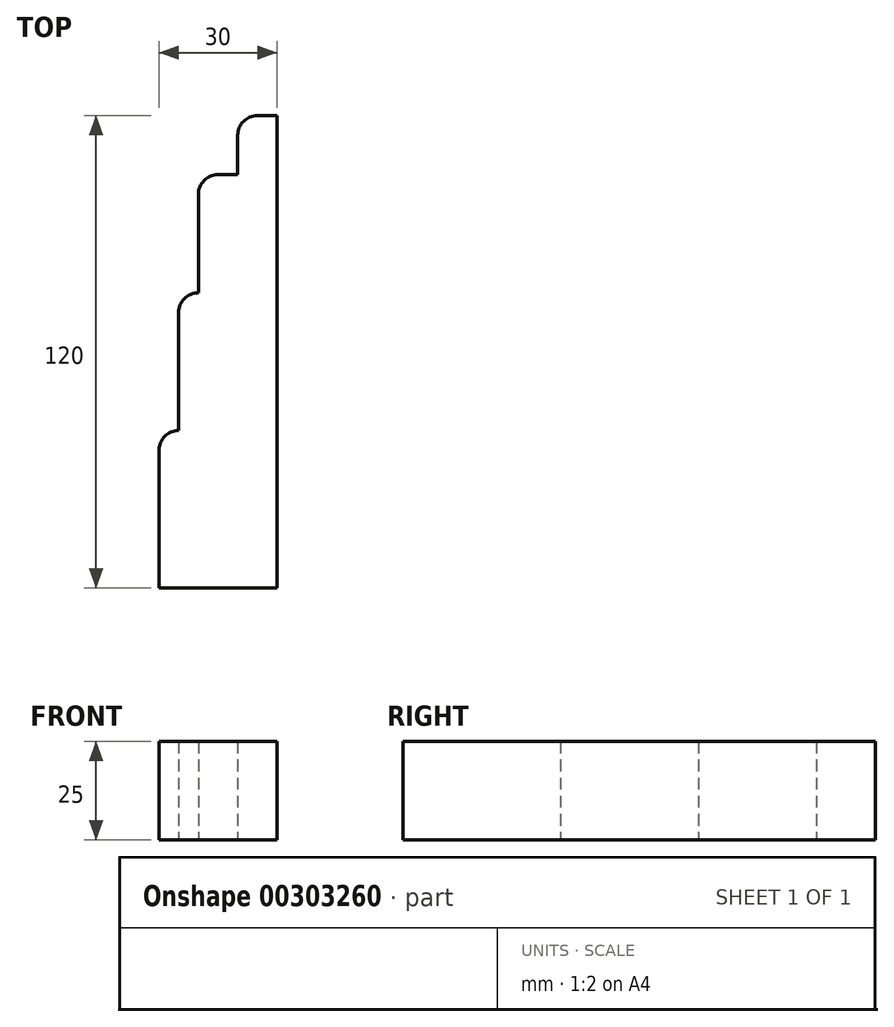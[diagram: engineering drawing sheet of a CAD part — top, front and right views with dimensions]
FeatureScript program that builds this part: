
annotation { "Feature Type Name" : "Feature", "Feature Type Description" : "" }
export const myFeature = defineFeature(function(context is Context, id is Id, definition is map)
    precondition{}
    {
        {
            var Q0;
            Q0=qCreatedBy(makeId("Top.planeOp"),FACE);
            var sketch = newSketch(context, id + "F0", { "sketchPlane" : qUnion([Q0])});
            skLineSegment(sketch, "E0", {"start": v(0, 0) * mm, "end": v(30, 0) * mm});
            skLineSegment(sketch, "E1", {"start": v(30, 0) * mm, "end": v(30, 120) * mm});
            skLineSegment(sketch, "E2", {"start": v(30, 120) * mm, "end": v(25, 120) * mm});
            skLineSegment(sketch, "E3", {"start": v(0, 0) * mm, "end": v(0, 35) * mm});
            skLineSegment(sketch, "E4", {"start": v(5, 40) * mm, "end": v(5, 40) * mm});
            skLineSegment(sketch, "E5", {"start": v(5, 40) * mm, "end": v(5, 70) * mm});
            skLineSegment(sketch, "E6", {"start": v(10, 75) * mm, "end": v(10, 75) * mm});
            skLineSegment(sketch, "E7", {"start": v(10, 75) * mm, "end": v(10, 100) * mm});
            skLineSegment(sketch, "E8", {"start": v(15, 105) * mm, "end": v(20, 105) * mm});
            skLineSegment(sketch, "E9", {"start": v(20, 105) * mm, "end": v(20, 115) * mm});
            skPoint(sketch, "E10.visualSharp", {"position": v(0, 40) * mm});
            skArc(sketch, "E10.filletArc", {"start": v(5, 40) * mm, "mid": v(1.46, 38.54) * mm, "end": v(0, 35) * mm});
            skPoint(sketch, "E11.visualSharp", {"position": v(5, 75) * mm});
            skArc(sketch, "E11.filletArc", {"start": v(10, 75) * mm, "mid": v(6.46, 73.54) * mm, "end": v(5, 70) * mm});
            skPoint(sketch, "E12.visualSharp", {"position": v(10, 105) * mm});
            skArc(sketch, "E12.filletArc", {"start": v(15, 105) * mm, "mid": v(11.46, 103.54) * mm, "end": v(10, 100) * mm});
            skPoint(sketch, "E13.visualSharp", {"position": v(20, 120) * mm});
            skArc(sketch, "E13.filletArc", {"start": v(25, 120) * mm, "mid": v(21.46, 118.54) * mm, "end": v(20, 115) * mm});
            skSolve(sketch);
        }
        {
            var Q0;
            Q0 = qSketchRegion(id + "F0", true);
            extrude(context, id + "F1", {"entities" : qUnion([Q0]), "depth" : 25 * mm});
        }
    });
